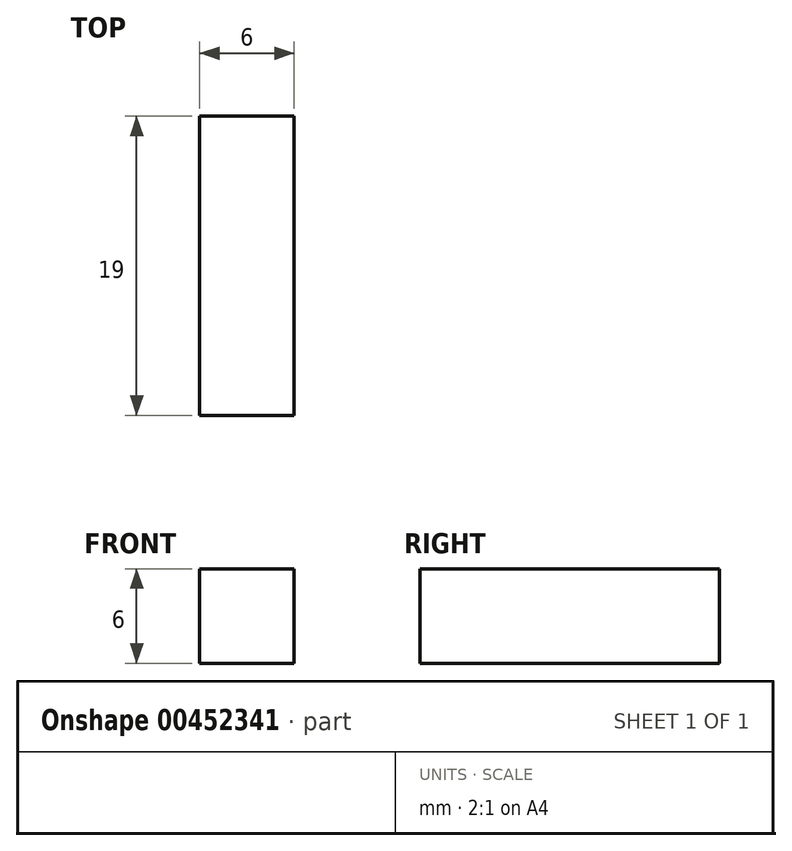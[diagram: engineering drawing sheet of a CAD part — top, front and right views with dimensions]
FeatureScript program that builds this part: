
annotation { "Feature Type Name" : "Feature", "Feature Type Description" : "" }
export const myFeature = defineFeature(function(context is Context, id is Id, definition is map)
    precondition{}
    {
        {
            var Q0;
            Q0=qCreatedBy(makeId("Front.planeOp"),FACE);
            var sketch = newSketch(context, id + "F0", { "sketchPlane" : qUnion([Q0])});
            skLineSegment(sketch, "E0.bottom", {"start": v(3, -3) * mm, "end": v(-3, -3) * mm});
            skLineSegment(sketch, "E0.top", {"start": v(3, 3) * mm, "end": v(-3, 3) * mm});
            skLineSegment(sketch, "E0.left", {"start": v(3, -3) * mm, "end": v(3, 3) * mm});
            skLineSegment(sketch, "E0.right", {"start": v(-3, -3) * mm, "end": v(-3, 3) * mm});
            skPoint(sketch, "E0.middle", {"position": v(0, 0) * mm});
            skSolve(sketch);
        }
        {
            var Q0;
            Q0 = qSketchRegion(id + "F0", true);
            extrude(context, id + "F1", {"entities" : qUnion([Q0]), "depth" : 19 * mm});
        }
    });
